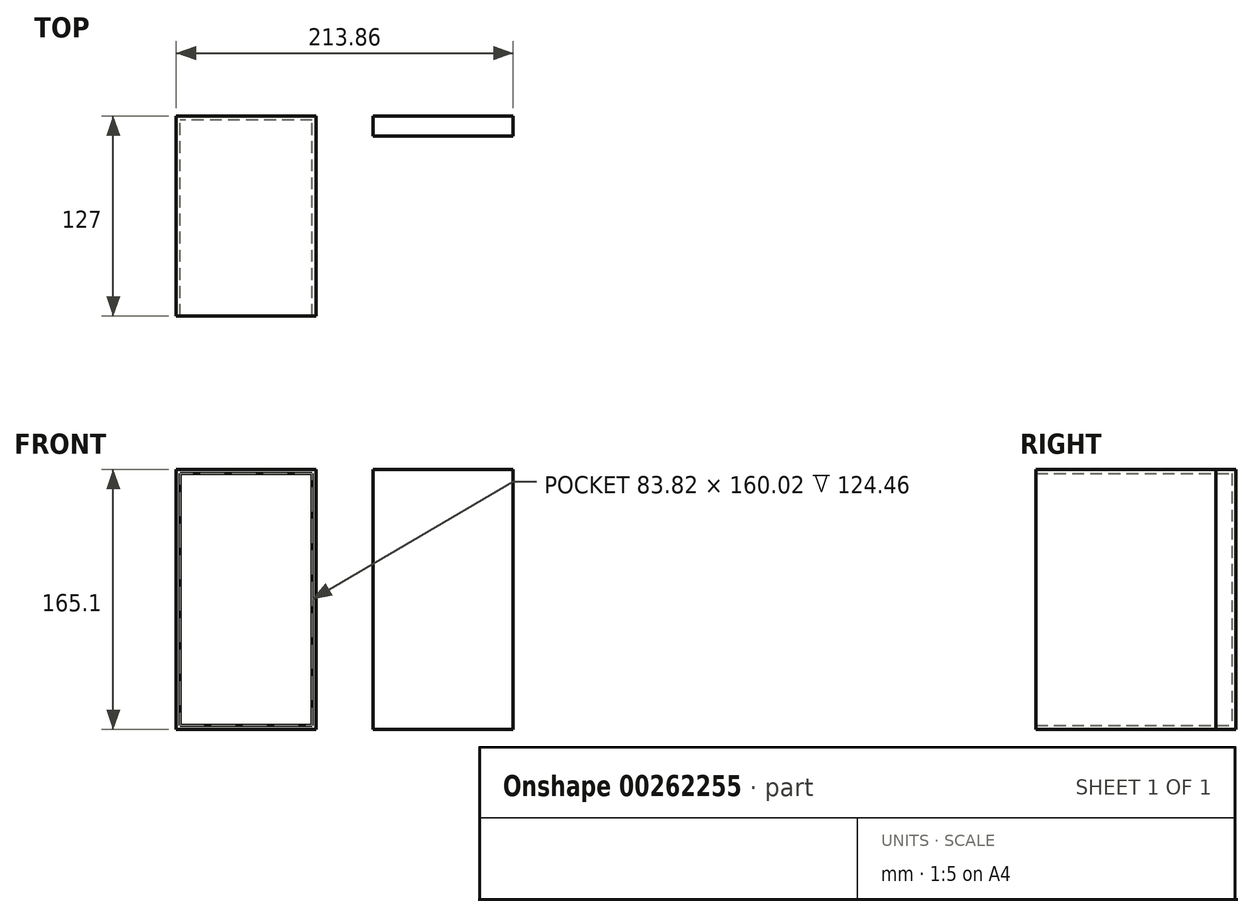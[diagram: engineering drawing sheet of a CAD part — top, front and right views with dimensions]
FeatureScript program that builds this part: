
annotation { "Feature Type Name" : "Feature", "Feature Type Description" : "" }
export const myFeature = defineFeature(function(context is Context, id is Id, definition is map)
    precondition{}
    {
        {
            var Q0;
            Q0=qCreatedBy(makeId("Front.planeOp"),FACE);
            var sketch = newSketch(context, id + "F0", { "sketchPlane" : qUnion([Q0])});
            skLineSegment(sketch, "E0.bottom", {"start": v(44.45, 82.55) * mm, "end": v(-44.45, 82.55) * mm});
            skLineSegment(sketch, "E0.top", {"start": v(44.45, -82.55) * mm, "end": v(-44.45, -82.55) * mm});
            skLineSegment(sketch, "E0.left", {"start": v(44.45, 82.55) * mm, "end": v(44.45, -82.55) * mm});
            skLineSegment(sketch, "E0.right", {"start": v(-44.45, 82.55) * mm, "end": v(-44.45, -82.55) * mm});
            skPoint(sketch, "E0.middle", {"position": v(0, 0) * mm});
            skLineSegment(sketch, "E1.bottom", {"start": v(169.41, 82.55) * mm, "end": v(80.51, 82.55) * mm});
            skLineSegment(sketch, "E1.top", {"start": v(169.41, -82.55) * mm, "end": v(80.51, -82.55) * mm});
            skLineSegment(sketch, "E1.left", {"start": v(169.41, 82.55) * mm, "end": v(169.41, -82.55) * mm});
            skLineSegment(sketch, "E1.right", {"start": v(80.51, 82.55) * mm, "end": v(80.51, -82.55) * mm});
            skPoint(sketch, "E1.middle", {"position": v(124.96, 0) * mm});
            skSolve(sketch);
        }
        {
            var Q0;
            Q0=makeQuery(id+"F0.imprint","IMPRINT",FACE,{"disambiguationData":[TD([[makeQuery(id+"F0.imprint","IMPRINT",EDGE,{"derivedFrom":sQuery(id+"F0.wireOp",EDGE,"E0.bottom")}),1.0]])]});
            extrude(context, id + "F1", {"entities" : qUnion([Q0]), "depth" : 127 * mm});
        }
        {
            var Q0;
            Q0=makeQuery(id+"F0.imprint","IMPRINT",FACE,{"disambiguationData":[TD([[makeQuery(id+"F0.imprint","IMPRINT",EDGE,{"derivedFrom":sQuery(id+"F0.wireOp",EDGE,"E1.bottom")}),1.0]])]});
            extrude(context, id + "F2", {"entities" : qUnion([Q0]), "depth" : 12.7 * mm});
        }
        {
            var Q0;
            Q0=makeQuery(id+"F1.opExtrude","CAP_FACE",FACE,{"disambiguationData":[OSD([sQuery(id+"F0.wireOp",EDGE,"E0.bottom"),sQuery(id+"F0.wireOp",EDGE,"E0.top"),sQuery(id+"F0.wireOp",EDGE,"E0.left"),sQuery(id+"F0.wireOp",EDGE,"E0.right")])],"isStart":false});
            shell(context, id + "F3", {"entities" : qUnion([Q0]), "thickness" : 2.54 * mm});
        }
    });
